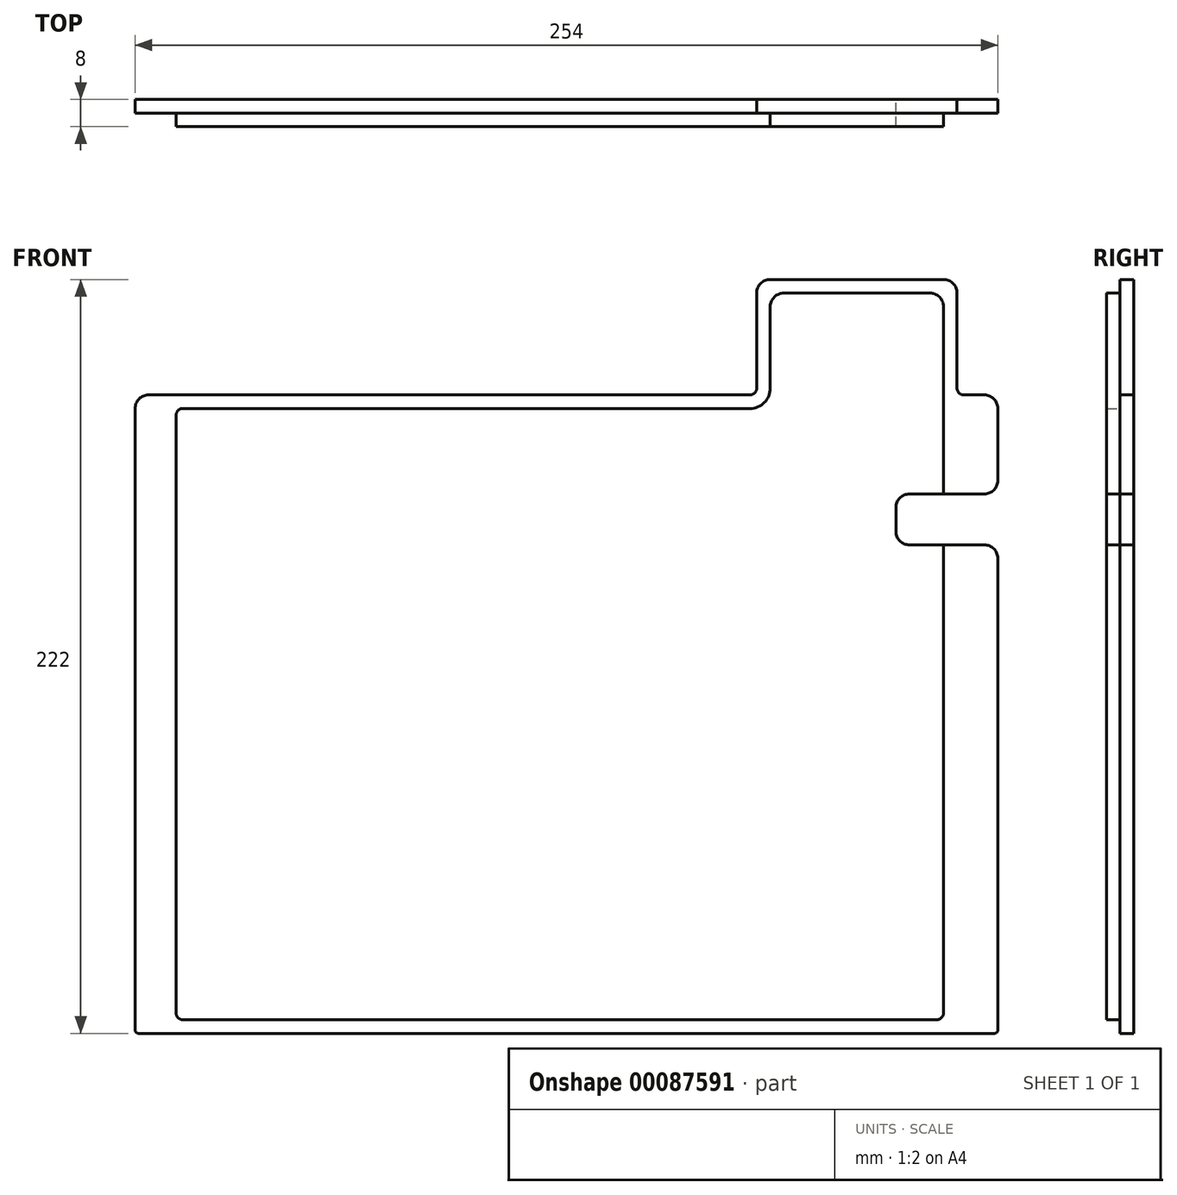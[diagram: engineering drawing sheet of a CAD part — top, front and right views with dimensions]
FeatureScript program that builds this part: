
annotation { "Feature Type Name" : "Feature", "Feature Type Description" : "" }
export const myFeature = defineFeature(function(context is Context, id is Id, definition is map)
    precondition{}
    {
        {
            var Q0;
            Q0=qCreatedBy(makeId("Front.planeOp"),FACE);
            var sketch = newSketch(context, id + "F0", { "sketchPlane" : qUnion([Q0])});
            skLineSegment(sketch, "E0.bottom", {"start": v(123, 94) * mm, "end": v(117, 94) * mm});
            skLineSegment(sketch, "E0.top", {"start": v(126, -94) * mm, "end": v(-126, -94) * mm});
            skLineSegment(sketch, "E0.left", {"start": v(127, 90) * mm, "end": v(127, 68.84) * mm});
            skLineSegment(sketch, "E0.right", {"start": v(-127, 90) * mm, "end": v(-127, -93) * mm});
            skPoint(sketch, "E0.middle", {"position": v(0, 0) * mm});
            skLineSegment(sketch, "E1.top", {"start": v(111, 128) * mm, "end": v(60, 128) * mm});
            skLineSegment(sketch, "E1.left", {"start": v(115, 96) * mm, "end": v(115, 124) * mm});
            skLineSegment(sketch, "E1.right", {"start": v(56, 96) * mm, "end": v(56, 124) * mm});
            skLineSegment(sketch, "E2.trimOffspring", {"start": v(54, 94) * mm, "end": v(-123, 94) * mm});
            skPoint(sketch, "E3.visualSharp", {"position": v(56, 128) * mm});
            skArc(sketch, "E3.filletArc", {"start": v(60, 128) * mm, "mid": v(57.17, 126.83) * mm, "end": v(56, 124) * mm});
            skPoint(sketch, "E4.visualSharp", {"position": v(115, 128) * mm});
            skArc(sketch, "E4.filletArc", {"start": v(115, 124) * mm, "mid": v(113.83, 126.83) * mm, "end": v(111, 128) * mm});
            skPoint(sketch, "E5.visualSharp", {"position": v(127, 94) * mm});
            skArc(sketch, "E5.filletArc", {"start": v(127, 90) * mm, "mid": v(125.83, 92.83) * mm, "end": v(123, 94) * mm});
            skPoint(sketch, "E6.visualSharp", {"position": v(-127, 94) * mm});
            skArc(sketch, "E6.filletArc", {"start": v(-123, 94) * mm, "mid": v(-125.83, 92.83) * mm, "end": v(-127, 90) * mm});
            skPoint(sketch, "E7.visualSharp", {"position": v(56, 94) * mm});
            skArc(sketch, "E7.filletArc", {"start": v(54, 94) * mm, "mid": v(55.41, 94.59) * mm, "end": v(56, 96) * mm});
            skPoint(sketch, "E8.visualSharp", {"position": v(115, 94) * mm});
            skArc(sketch, "E8.filletArc", {"start": v(115, 96) * mm, "mid": v(115.59, 94.59) * mm, "end": v(117, 94) * mm});
            skPoint(sketch, "E9.visualSharp", {"position": v(-127, -94) * mm});
            skArc(sketch, "E9.filletArc", {"start": v(-127, -93) * mm, "mid": v(-126.7, -93.7) * mm, "end": v(-126, -94) * mm});
            skPoint(sketch, "E10.visualSharp", {"position": v(127, -94) * mm});
            skArc(sketch, "E10.filletArc", {"start": v(126, -94) * mm, "mid": v(126.7, -93.7) * mm, "end": v(127, -93) * mm});
            skLineSegment(sketch, "E11.bottom", {"start": v(123, 64.84) * mm, "end": v(101, 64.84) * mm});
            skLineSegment(sketch, "E11.top", {"start": v(123, 49.84) * mm, "end": v(101, 49.84) * mm});
            skLineSegment(sketch, "E11.right", {"start": v(97, 60.84) * mm, "end": v(97, 53.84) * mm});
            skLineSegment(sketch, "E12.trimOffspring", {"start": v(127, 45.84) * mm, "end": v(127, -93) * mm});
            skPoint(sketch, "E13.visualSharp", {"position": v(97, 64.84) * mm});
            skArc(sketch, "E13.filletArc", {"start": v(101, 64.84) * mm, "mid": v(98.17, 63.67) * mm, "end": v(97, 60.84) * mm});
            skPoint(sketch, "E14.visualSharp", {"position": v(97, 49.84) * mm});
            skArc(sketch, "E14.filletArc", {"start": v(97, 53.84) * mm, "mid": v(98.17, 51.01) * mm, "end": v(101, 49.84) * mm});
            skPoint(sketch, "E15.visualSharp", {"position": v(127, 64.84) * mm});
            skArc(sketch, "E15.filletArc", {"start": v(123, 64.84) * mm, "mid": v(125.83, 66.01) * mm, "end": v(127, 68.84) * mm});
            skPoint(sketch, "E16.visualSharp", {"position": v(127, 49.84) * mm});
            skArc(sketch, "E16.filletArc", {"start": v(127, 45.84) * mm, "mid": v(125.83, 48.67) * mm, "end": v(123, 49.84) * mm});
            skSolve(sketch);
        }
        {
            var Q0;
            Q0=makeQuery(id+"F0.imprint","IMPRINT",FACE,{"disambiguationData":[TD([[makeQuery(id+"F0.imprint","IMPRINT",EDGE,{"derivedFrom":sQuery(id+"F0.wireOp",EDGE,"E0.bottom")}),1.0]])]});
            extrude(context, id + "F1", {"entities" : qUnion([Q0]), "depth" : 4 * mm});
        }
        {
            var Q0;
            Q0=makeQuery(id+"F1.opExtrude","CAP_FACE",FACE,{"disambiguationData":[OSD([sQuery(id+"F0.wireOp",EDGE,"E0.bottom"),sQuery(id+"F0.wireOp",EDGE,"E0.top"),sQuery(id+"F0.wireOp",EDGE,"E0.left"),sQuery(id+"F0.wireOp",EDGE,"E0.right"),sQuery(id+"F0.wireOp",EDGE,"E1.top"),sQuery(id+"F0.wireOp",EDGE,"E1.left"),sQuery(id+"F0.wireOp",EDGE,"E1.right"),sQuery(id+"F0.wireOp",EDGE,"E2.trimOffspring"),sQuery(id+"F0.wireOp",EDGE,"E3.filletArc"),sQuery(id+"F0.wireOp",EDGE,"E4.filletArc"),sQuery(id+"F0.wireOp",EDGE,"E5.filletArc"),sQuery(id+"F0.wireOp",EDGE,"E6.filletArc"),sQuery(id+"F0.wireOp",EDGE,"E7.filletArc"),sQuery(id+"F0.wireOp",EDGE,"E8.filletArc"),sQuery(id+"F0.wireOp",EDGE,"E9.filletArc"),sQuery(id+"F0.wireOp",EDGE,"E10.filletArc")])],"isStart":false});
            var sketch = newSketch(context, id + "F2", { "sketchPlane" : qUnion([Q0])});
            skLineSegment(sketch, "E17.0", {"start": v(123, 94) * mm, "end": v(117, 94) * mm, "construction": true});
            skLineSegment(sketch, "E17.1", {"start": v(126, -94) * mm, "end": v(-126, -94) * mm, "construction": true});
            skLineSegment(sketch, "E17.2", {"start": v(127, 90) * mm, "end": v(127, 68.84) * mm, "construction": true});
            skLineSegment(sketch, "E17.3", {"start": v(-127, 90) * mm, "end": v(-127, -93) * mm, "construction": true});
            skPoint(sketch, "E17.4", {"position": v(0, 0) * mm});
            skLineSegment(sketch, "E17.5", {"start": v(111, 128) * mm, "end": v(60, 128) * mm, "construction": true});
            skLineSegment(sketch, "E17.6", {"start": v(115, 96) * mm, "end": v(115, 124) * mm, "construction": true});
            skLineSegment(sketch, "E17.7", {"start": v(56, 96) * mm, "end": v(56, 124) * mm, "construction": true});
            skLineSegment(sketch, "E17.8", {"start": v(54, 94) * mm, "end": v(-123, 94) * mm, "construction": true});
            skPoint(sketch, "E17.9", {"position": v(56, 128) * mm});
            skArc(sketch, "E17.10", {"start": v(60, 128) * mm, "mid": v(57.17, 126.83) * mm, "end": v(56, 124) * mm, "construction": true});
            skPoint(sketch, "E17.11", {"position": v(115, 128) * mm});
            skArc(sketch, "E17.12", {"start": v(115, 124) * mm, "mid": v(113.83, 126.83) * mm, "end": v(111, 128) * mm, "construction": true});
            skPoint(sketch, "E17.13", {"position": v(127, 94) * mm});
            skArc(sketch, "E17.14", {"start": v(127, 90) * mm, "mid": v(125.83, 92.83) * mm, "end": v(123, 94) * mm, "construction": true});
            skPoint(sketch, "E17.15", {"position": v(-127, 94) * mm});
            skArc(sketch, "E17.16", {"start": v(-123, 94) * mm, "mid": v(-125.83, 92.83) * mm, "end": v(-127, 90) * mm, "construction": true});
            skPoint(sketch, "E17.17", {"position": v(56, 94) * mm});
            skArc(sketch, "E17.18", {"start": v(54, 94) * mm, "mid": v(55.41, 94.59) * mm, "end": v(56, 96) * mm, "construction": true});
            skPoint(sketch, "E17.19", {"position": v(115, 94) * mm});
            skArc(sketch, "E17.20", {"start": v(115, 96) * mm, "mid": v(115.59, 94.59) * mm, "end": v(117, 94) * mm, "construction": true});
            skPoint(sketch, "E17.21", {"position": v(-127, -94) * mm});
            skArc(sketch, "E17.22", {"start": v(-127, -93) * mm, "mid": v(-126.7, -93.7) * mm, "end": v(-126, -94) * mm, "construction": true});
            skPoint(sketch, "E17.23", {"position": v(127, -94) * mm});
            skArc(sketch, "E17.24", {"start": v(126, -94) * mm, "mid": v(126.7, -93.7) * mm, "end": v(127, -93) * mm, "construction": true});
            skArc(sketch, "E18.0", {"start": v(54, 90) * mm, "mid": v(58.24, 91.76) * mm, "end": v(60, 96) * mm});
            skLineSegment(sketch, "E18.1", {"start": v(54, 90) * mm, "end": v(-112.94, 90) * mm});
            skLineSegment(sketch, "E18.2", {"start": v(60, 96) * mm, "end": v(60, 120) * mm});
            skLineSegment(sketch, "E18.4", {"start": v(109, -90) * mm, "end": v(-112.94, -90) * mm});
            skLineSegment(sketch, "E18.6", {"start": v(107, 124) * mm, "end": v(64, 124) * mm});
            skLineSegment(sketch, "E18.7", {"start": v(111, 96) * mm, "end": v(111, 120) * mm});
            skLineSegment(sketch, "E19", {"start": v(-114.94, 88) * mm, "end": v(-114.94, -88) * mm});
            skLineSegment(sketch, "E20", {"start": v(111, 96) * mm, "end": v(111, 64.84) * mm});
            skPoint(sketch, "E21.visualSharp", {"position": v(-114.94, 90) * mm});
            skArc(sketch, "E21.filletArc", {"start": v(-112.94, 90) * mm, "mid": v(-114.35, 89.41) * mm, "end": v(-114.94, 88) * mm});
            skPoint(sketch, "E22.visualSharp", {"position": v(-114.94, -90) * mm});
            skArc(sketch, "E22.filletArc", {"start": v(-114.94, -88) * mm, "mid": v(-114.35, -89.41) * mm, "end": v(-112.94, -90) * mm});
            skPoint(sketch, "E23.visualSharp", {"position": v(111, -90) * mm});
            skArc(sketch, "E23.filletArc", {"start": v(109, -90) * mm, "mid": v(110.41, -89.41) * mm, "end": v(111, -88) * mm});
            skArc(sketch, "E24.filletArc", {"start": v(64, 124) * mm, "mid": v(61.17, 122.83) * mm, "end": v(60, 120) * mm});
            skArc(sketch, "E25.filletArc", {"start": v(111, 120) * mm, "mid": v(109.83, 122.83) * mm, "end": v(107, 124) * mm});
            skLineSegment(sketch, "E26.0", {"start": v(111, 64.84) * mm, "end": v(101, 64.84) * mm});
            skArc(sketch, "E26.1", {"start": v(101, 64.84) * mm, "mid": v(98.17, 63.67) * mm, "end": v(97, 60.84) * mm});
            skLineSegment(sketch, "E26.2", {"start": v(97, 60.84) * mm, "end": v(97, 53.84) * mm});
            skArc(sketch, "E26.3", {"start": v(97, 53.84) * mm, "mid": v(98.17, 51.01) * mm, "end": v(101, 49.84) * mm});
            skLineSegment(sketch, "E26.4", {"start": v(111, 49.84) * mm, "end": v(101, 49.84) * mm});
            skPoint(sketch, "E27.orphan", {"position": v(123, 64.84) * mm});
            skPoint(sketch, "E28.orphan", {"position": v(123, 49.84) * mm});
            skLineSegment(sketch, "E29.trimOffspring", {"start": v(111, 49.84) * mm, "end": v(111, -88) * mm});
            skSolve(sketch);
        }
        {
            var Q0;
            Q0 = qSketchRegion(id + "F2", true);
            extrude(context, id + "F3", {"entities" : qUnion([Q0]), "depth" : 4 * mm});
        }
    });
